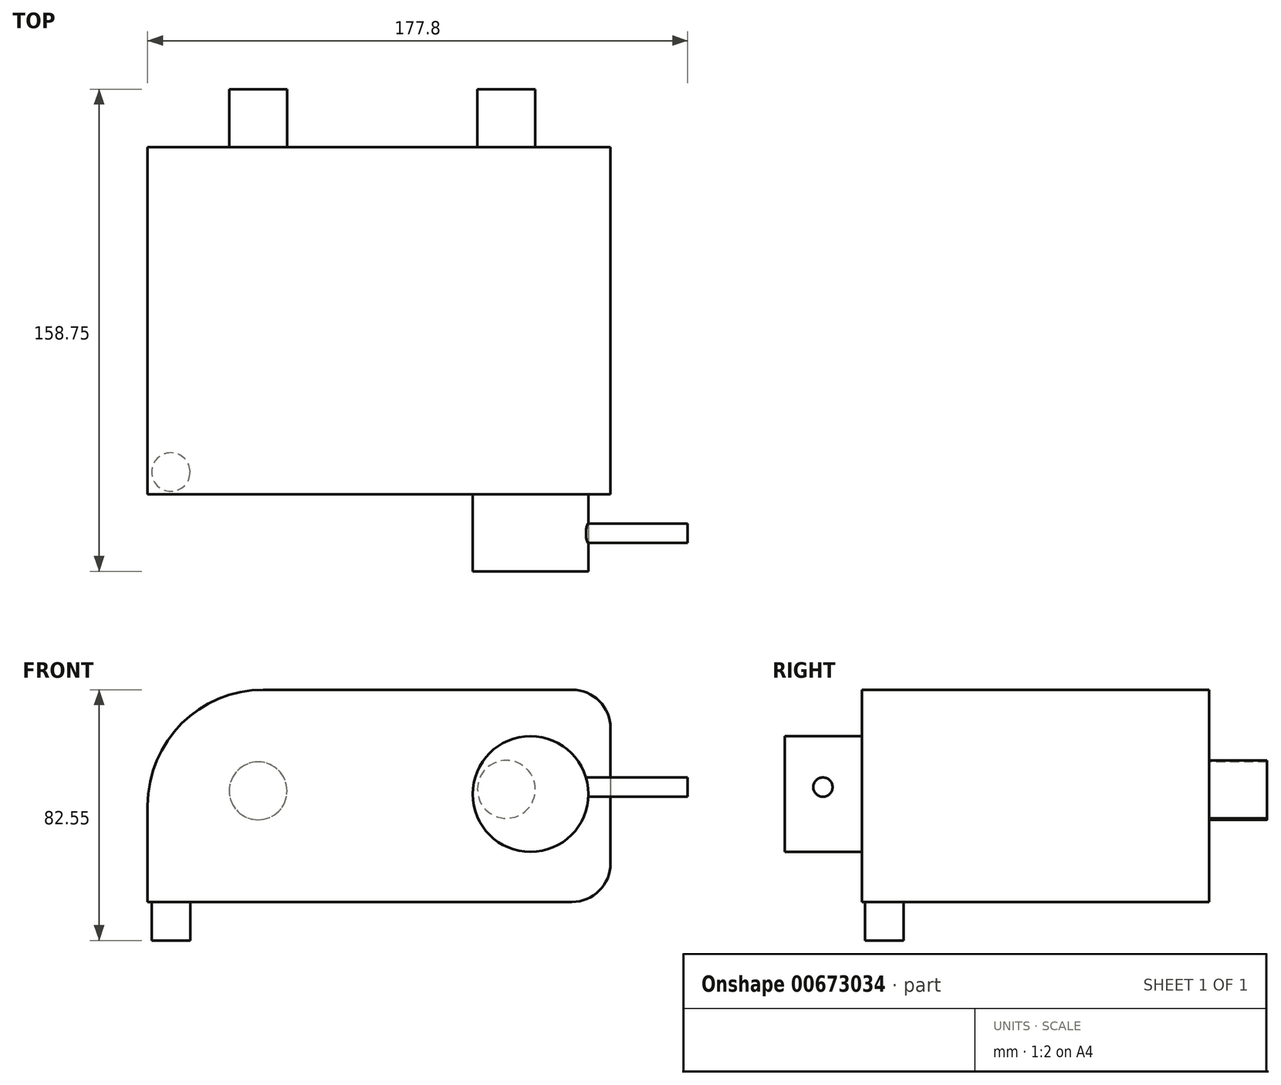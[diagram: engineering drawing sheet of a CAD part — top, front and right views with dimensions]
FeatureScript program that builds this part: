
annotation { "Feature Type Name" : "Feature", "Feature Type Description" : "" }
export const myFeature = defineFeature(function(context is Context, id is Id, definition is map)
    precondition{}
    {
        {
            var Q0;
            Q0=qCreatedBy(makeId("Front.planeOp"),FACE);
            var sketch = newSketch(context, id + "F0", { "sketchPlane" : qUnion([Q0])});
            skLineSegment(sketch, "E0.bottom", {"start": v(38.1, 0) * mm, "end": v(139.7, 0) * mm});
            skLineSegment(sketch, "E0.top", {"start": v(0, -69.85) * mm, "end": v(139.7, -69.85) * mm});
            skLineSegment(sketch, "E0.left", {"start": v(0, -38.1) * mm, "end": v(0, -69.85) * mm});
            skLineSegment(sketch, "E0.right", {"start": v(152.4, -12.7) * mm, "end": v(152.4, -57.15) * mm});
            skPoint(sketch, "E1.visualSharp", {"position": v(0, 0) * mm});
            skArc(sketch, "E1.filletArc", {"start": v(38.1, 0) * mm, "mid": v(11.16, -11.16) * mm, "end": v(0, -38.1) * mm});
            skPoint(sketch, "E2.visualSharp", {"position": v(152.4, 0) * mm});
            skArc(sketch, "E2.filletArc", {"start": v(152.4, -12.7) * mm, "mid": v(148.68, -3.72) * mm, "end": v(139.7, 0) * mm});
            skPoint(sketch, "E3.visualSharp", {"position": v(152.4, -69.85) * mm});
            skArc(sketch, "E3.filletArc", {"start": v(139.7, -69.85) * mm, "mid": v(148.68, -66.13) * mm, "end": v(152.4, -57.15) * mm});
            skSolve(sketch);
        }
        {
            var Q0;
            Q0=makeQuery(id+"F0.imprint","IMPRINT",FACE,{"disambiguationData":[TD([[makeQuery(id+"F0.imprint","IMPRINT",EDGE,{"derivedFrom":sQuery(id+"F0.wireOp",EDGE,"E0.bottom")}),-1.0]])]});
            extrude(context, id + "F1", {"entities" : qUnion([Q0]), "depth" : 114.3 * mm, "offsetDistance" : 25.4 * mm});
        }
        {
            var Q0;
            Q0=makeQuery(id+"F1.opExtrude","CAP_FACE",FACE,{"disambiguationData":[OSD([sQuery(id+"F0.wireOp",EDGE,"E0.bottom"),sQuery(id+"F0.wireOp",EDGE,"E0.top"),sQuery(id+"F0.wireOp",EDGE,"E0.left"),sQuery(id+"F0.wireOp",EDGE,"E0.right"),sQuery(id+"F0.wireOp",EDGE,"E1.filletArc"),sQuery(id+"F0.wireOp",EDGE,"E2.filletArc"),sQuery(id+"F0.wireOp",EDGE,"E3.filletArc")])],"isStart":false});
            var sketch = newSketch(context, id + "F2", { "sketchPlane" : qUnion([Q0])});
            skCircle(sketch, "E4", {"center": v(126.04, -34.36) * mm, "radius": 19.05 * mm});
            skSolve(sketch);
        }
        {
            var Q0;
            Q0 = qSketchRegion(id + "F2", true);
            extrude(context, id + "F3", {"entities" : qUnion([Q0]), "operationType" : NewBodyOperationType.ADD, "depth" : 25.4 * mm, "offsetDistance" : 25.4 * mm});
        }
        {
            var Q0;
            Q0=makeQuery(id+"F1.opExtrude","SWEPT_FACE",FACE,{"disambiguationData":[OSD([sQuery(id+"F0.wireOp",EDGE,"E0.top")])]});
            var sketch = newSketch(context, id + "F4", { "sketchPlane" : qUnion([Q0])});
            skCircle(sketch, "E5", {"center": v(7.62, 107.05) * mm, "radius": 6.35 * mm});
            skSolve(sketch);
        }
        {
            var Q0;
            Q0 = qSketchRegion(id + "F4", true);
            extrude(context, id + "F5", {"entities" : qUnion([Q0]), "operationType" : NewBodyOperationType.ADD, "depth" : 12.7 * mm, "offsetDistance" : 25.4 * mm});
        }
        {
            var Q0;
            Q0=makeQuery(id+"F1.opExtrude","SWEPT_FACE",FACE,{"disambiguationData":[OSD([sQuery(id+"F0.wireOp",EDGE,"E0.right")])]});
            var sketch = newSketch(context, id + "F6", { "sketchPlane" : qUnion([Q0])});
            skCircle(sketch, "E6", {"center": v(-127.2, -32.07) * mm, "radius": 3.18 * mm});
            skSolve(sketch);
        }
        {
            var Q0;
            Q0 = qSketchRegion(id + "F6", true);
            extrude(context, id + "F7", {"entities" : qUnion([Q0]), "operationType" : NewBodyOperationType.ADD, "oppositeDirection" : true, "depth" : 12.7 * mm, "offsetDistance" : 25.4 * mm});
        }
        {
            var Q0;
            Q0=makeQuery(id+"F7.opExtrude","CAP_FACE",FACE,{"disambiguationData":[OSD([sQuery(id+"F6.wireOp",EDGE,"E6")])],"isStart":true});
            extrude(context, id + "F8", {"entities" : qUnion([Q0]), "operationType" : NewBodyOperationType.ADD, "depth" : 25.4 * mm, "offsetDistance" : 25.4 * mm});
        }
        {
            var Q0;
            Q0=makeQuery(id+"F1.opExtrude","CAP_FACE",FACE,{"disambiguationData":[OSD([sQuery(id+"F0.wireOp",EDGE,"E0.bottom"),sQuery(id+"F0.wireOp",EDGE,"E0.top"),sQuery(id+"F0.wireOp",EDGE,"E0.left"),sQuery(id+"F0.wireOp",EDGE,"E0.right"),sQuery(id+"F0.wireOp",EDGE,"E1.filletArc"),sQuery(id+"F0.wireOp",EDGE,"E2.filletArc"),sQuery(id+"F0.wireOp",EDGE,"E3.filletArc")])],"isStart":true});
            var sketch = newSketch(context, id + "F9", { "sketchPlane" : qUnion([Q0])});
            skCircle(sketch, "E7", {"center": v(-118.1, -32.8) * mm, "radius": 9.53 * mm});
            skCircle(sketch, "E8", {"center": v(-36.35, -33.3) * mm, "radius": 9.53 * mm});
            skSolve(sketch);
        }
        {
            var Q0;
            Q0 = qSketchRegion(id + "F9", true);
            extrude(context, id + "F10", {"entities" : qUnion([Q0]), "operationType" : NewBodyOperationType.ADD, "depth" : 19.05 * mm, "offsetDistance" : 25.4 * mm});
        }
    });
